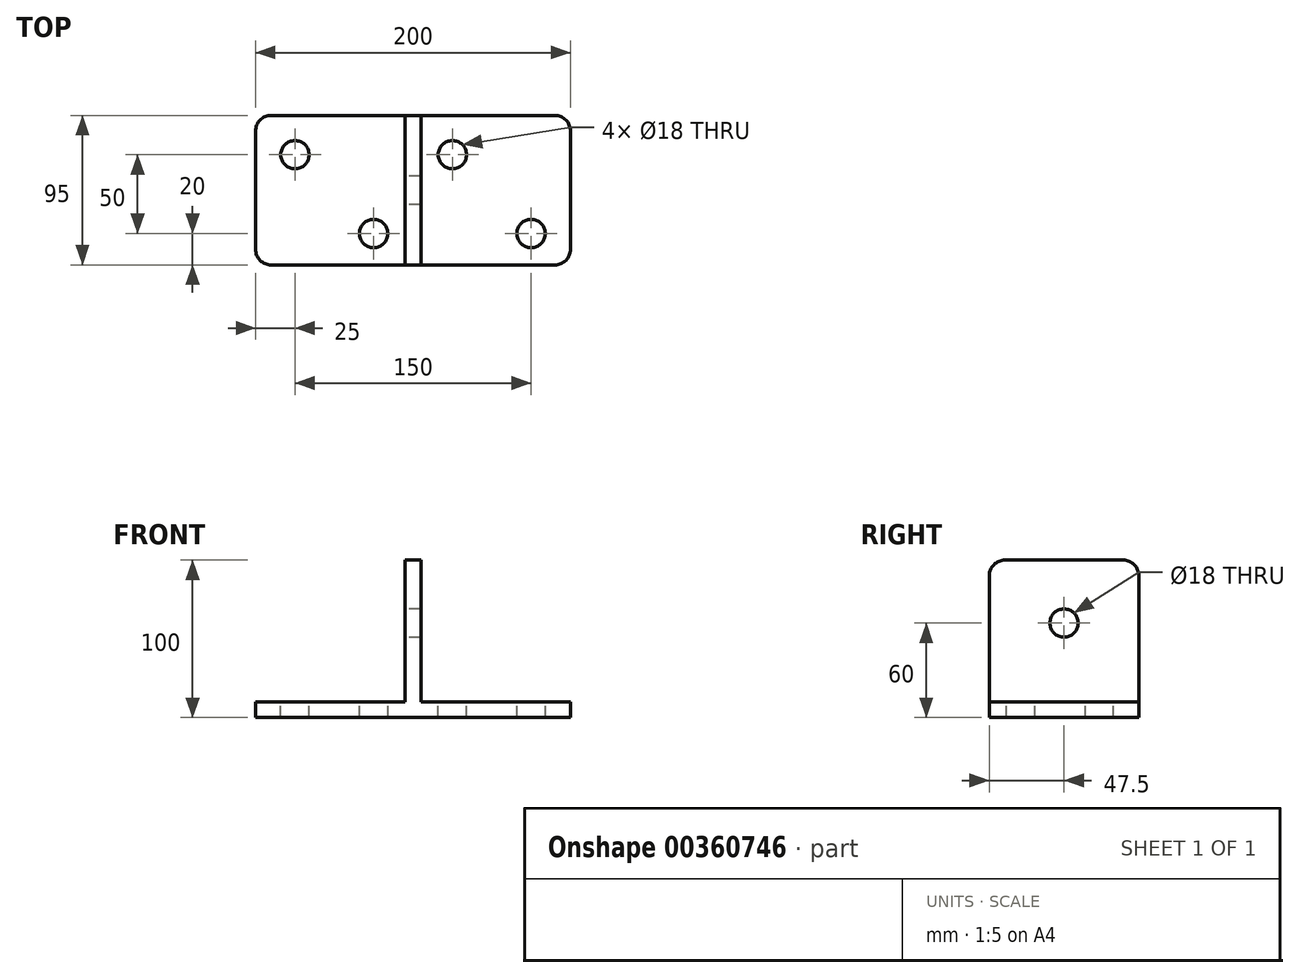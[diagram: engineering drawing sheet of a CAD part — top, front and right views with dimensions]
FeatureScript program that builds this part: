
annotation { "Feature Type Name" : "Feature", "Feature Type Description" : "" }
export const myFeature = defineFeature(function(context is Context, id is Id, definition is map)
    precondition{}
    {
        {
            var Q0;
            Q0=qCreatedBy(makeId("Front.planeOp"),FACE);
            var sketch = newSketch(context, id + "F0", { "sketchPlane" : qUnion([Q0])});
            skLineSegment(sketch, "E0", {"start": v(0, 0) * mm, "end": v(100, 0) * mm});
            skLineSegment(sketch, "E1", {"start": v(100, 0) * mm, "end": v(100, 10) * mm});
            skLineSegment(sketch, "E2", {"start": v(100, 10) * mm, "end": v(5, 10) * mm});
            skLineSegment(sketch, "E3", {"start": v(5, 10) * mm, "end": v(5, 100) * mm});
            skLineSegment(sketch, "E4", {"start": v(5, 100) * mm, "end": v(0, 100) * mm});
            skLineSegment(sketch, "E5.MirrorCS", {"start": v(-5, 100) * mm, "end": v(0, 100) * mm});
            skLineSegment(sketch, "E6.MirrorCS", {"start": v(-100, 0) * mm, "end": v(-100, 10) * mm});
            skLineSegment(sketch, "E7.MirrorCS", {"start": v(-100, 10) * mm, "end": v(-5, 10) * mm});
            skLineSegment(sketch, "E8.MirrorCS", {"start": v(0, 0) * mm, "end": v(-100, 0) * mm});
            skLineSegment(sketch, "E9.MirrorCS", {"start": v(-5, 10) * mm, "end": v(-5, 100) * mm});
            skSolve(sketch);
        }
        {
            var Q0;
            Q0=makeQuery(id+"F0.imprint","IMPRINT",FACE,{"disambiguationData":[TD([[makeQuery(id+"F0.imprint","IMPRINT",EDGE,{"derivedFrom":sQuery(id+"F0.wireOp",EDGE,"E0")}),1.0]])]});
            extrude(context, id + "F1", {"entities" : qUnion([Q0]), "endBound" : BoundingType.SYMMETRIC, "depth" : 95 * mm});
        }
        {
            var Q0;
            Q0=makeQuery(id+"F1.opExtrude","SWEPT_FACE",FACE,{"disambiguationData":[OSD([sQuery(id+"F0.wireOp",EDGE,"E2")])]});
            var sketch = newSketch(context, id + "F2", { "sketchPlane" : qUnion([Q0])});
            skCircle(sketch, "E10", {"center": v(75, -27.5) * mm, "radius": 9 * mm});
            skCircle(sketch, "E11", {"center": v(25, 22.5) * mm, "radius": 9 * mm});
            skCircle(sketch, "E12.MirrorC", {"center": v(-25, -27.5) * mm, "radius": 9 * mm});
            skCircle(sketch, "E13.MirrorC", {"center": v(-75, 22.5) * mm, "radius": 9 * mm});
            skSolve(sketch);
        }
        {
            var Q0;
            Q0=qSketchRegion(id+"F2",true);
            extrude(context, id + "F3", {"entities" : qUnion([Q0]), "operationType" : NewBodyOperationType.REMOVE, "oppositeDirection" : true, "depth" : 25 * mm});
        }
        {
            var Q0;
            Q0=makeQuery(id+"F1.opExtrude","SWEPT_FACE",FACE,{"disambiguationData":[OSD([sQuery(id+"F0.wireOp",EDGE,"E9.MirrorCS")])]});
            var sketch = newSketch(context, id + "F4", { "sketchPlane" : qUnion([Q0])});
            skCircle(sketch, "E14", {"center": v(0, 60) * mm, "radius": 9 * mm});
            skSolve(sketch);
        }
        {
            var Q0;
            Q0=qSketchRegion(id+"F4",true);
            extrude(context, id + "F5", {"entities" : qUnion([Q0]), "operationType" : NewBodyOperationType.REMOVE, "oppositeDirection" : true, "depth" : 25 * mm});
        }
        {
            var Q0;
            Q0=makeQuery(id+"F1.opExtrude","CAP_EDGE",EDGE,{"disambiguationData":[OSD([sQuery(id+"F0.wireOp",EDGE,"E4"),sQuery(id+"F0.wireOp",EDGE,"E5.MirrorCS")])],"isStart":false});
            var Q1;
            Q1=makeQuery(id+"F1.opExtrude","CAP_EDGE",EDGE,{"disambiguationData":[OSD([sQuery(id+"F0.wireOp",EDGE,"E4"),sQuery(id+"F0.wireOp",EDGE,"E5.MirrorCS")])],"isStart":true});
            var Q2;
            Q2=makeQuery(id+"F1.opExtrude","CAP_EDGE",EDGE,{"disambiguationData":[OSD([sQuery(id+"F0.wireOp",EDGE,"E6.MirrorCS")])],"isStart":true});
            var Q3;
            Q3=makeQuery(id+"F1.opExtrude","CAP_EDGE",EDGE,{"disambiguationData":[OSD([sQuery(id+"F0.wireOp",EDGE,"E6.MirrorCS")])],"isStart":false});
            var Q4;
            Q4=makeQuery(id+"F1.opExtrude","CAP_EDGE",EDGE,{"disambiguationData":[OSD([sQuery(id+"F0.wireOp",EDGE,"E1")])],"isStart":true});
            var Q5;
            Q5=makeQuery(id+"F1.opExtrude","CAP_EDGE",EDGE,{"disambiguationData":[OSD([sQuery(id+"F0.wireOp",EDGE,"E1")])],"isStart":false});
            fillet(context, id + "F6", {"entities" : qUnion([Q0, Q1, Q2, Q3, Q4, Q5]), "radius" : 10 * mm, "tangentPropagation" : true, "allowEdgeOverflow" : false});
        }
    });
